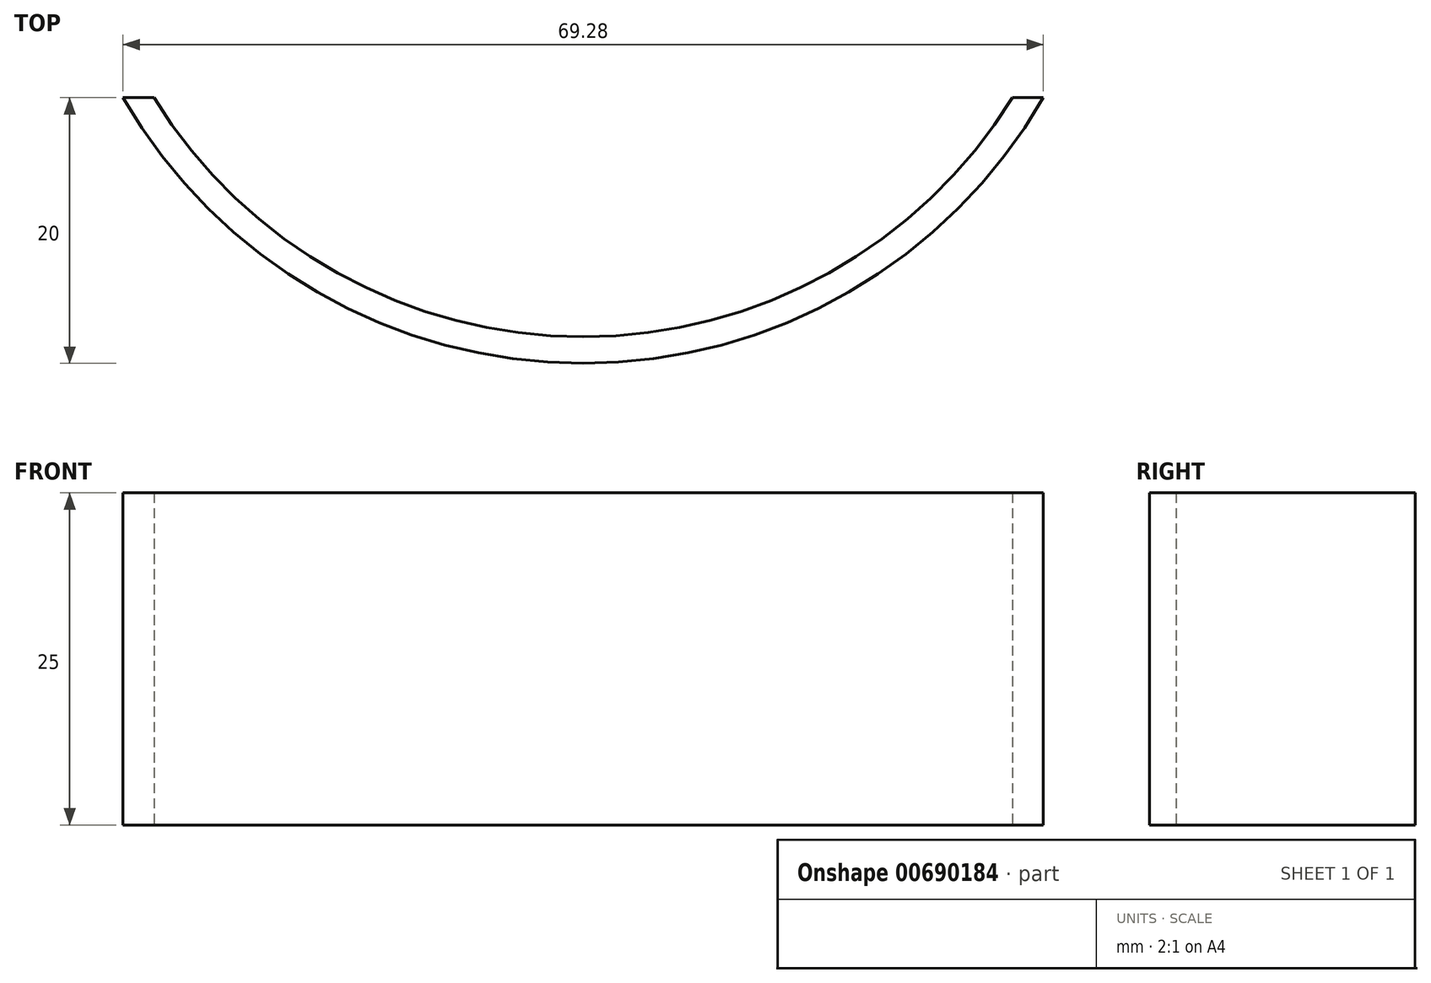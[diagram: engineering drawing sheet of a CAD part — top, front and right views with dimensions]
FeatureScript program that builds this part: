
annotation { "Feature Type Name" : "Feature", "Feature Type Description" : "" }
export const myFeature = defineFeature(function(context is Context, id is Id, definition is map)
    precondition{}
    {
        {
            var Q0;
            Q0=qCreatedBy(makeId("Top.planeOp"),FACE);
            var sketch = newSketch(context, id + "F0", { "sketchPlane" : qUnion([Q0])});
            skArc(sketch, "E0", {"start": v(-32.31, -20) * mm, "mid": v(0, -38) * mm, "end": v(32.31, -20) * mm});
            skArc(sketch, "E1", {"start": v(-34.64, -20) * mm, "mid": v(0, -40) * mm, "end": v(34.64, -20) * mm});
            skLineSegment(sketch, "E2", {"start": v(-34.64, -20) * mm, "end": v(-32.31, -20) * mm});
            skLineSegment(sketch, "E3.trimOffspring", {"start": v(32.31, -20) * mm, "end": v(34.64, -20) * mm});
            skSolve(sketch);
        }
        {
            var Q0;
            Q0=makeQuery(id+"F0.imprint","IMPRINT",FACE,{"disambiguationData":[TD([[makeQuery(id+"F0.imprint","IMPRINT",EDGE,{"derivedFrom":sQuery(id+"F0.wireOp",EDGE,"E0")}),-1.0]])]});
            extrude(context, id + "F1", {"entities" : qUnion([Q0]), "depth" : 25 * mm, "offsetDistance" : 25 * mm});
        }
    });
